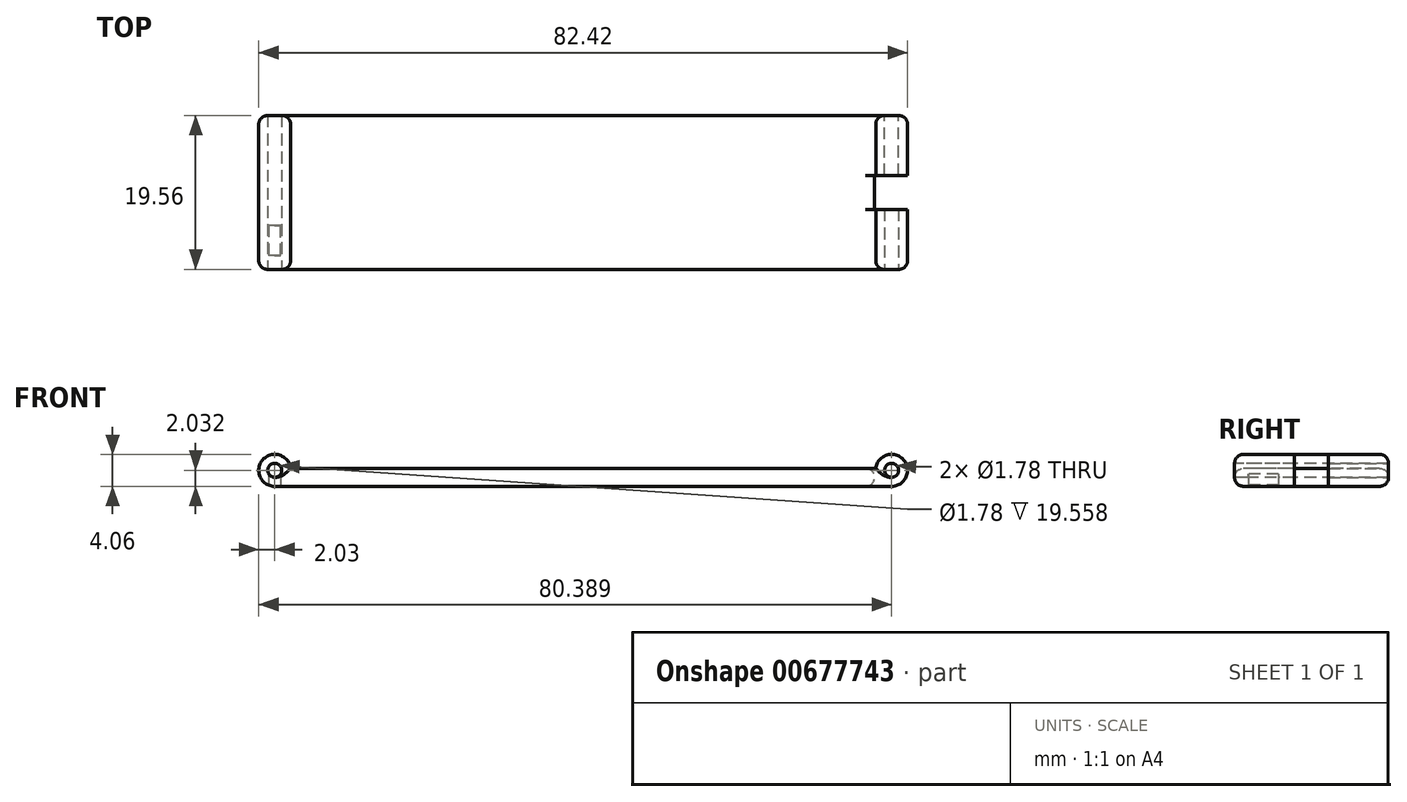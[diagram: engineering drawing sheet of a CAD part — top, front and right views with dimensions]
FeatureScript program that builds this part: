
annotation { "Feature Type Name" : "Feature", "Feature Type Description" : "" }
export const myFeature = defineFeature(function(context is Context, id is Id, definition is map)
    precondition{}
    {
        {
            var Q0;
            Q0=qCreatedBy(makeId("Top.planeOp"),FACE);
            var sketch = newSketch(context, id + "F0", { "sketchPlane" : qUnion([Q0])});
            skLineSegment(sketch, "E0.bottom", {"start": v(0, 0) * mm, "end": v(115.57, 0) * mm});
            skLineSegment(sketch, "E0.top", {"start": v(0, 19.56) * mm, "end": v(115.57, 19.56) * mm});
            skLineSegment(sketch, "E0.left", {"start": v(0, 0) * mm, "end": v(0, 19.56) * mm});
            skLineSegment(sketch, "E0.right", {"start": v(121.92, 6.35) * mm, "end": v(121.92, 13.2) * mm});
            skPoint(sketch, "E1.visualSharp", {"position": v(121.92, 19.56) * mm});
            skArc(sketch, "E1.filletArc", {"start": v(121.92, 13.2) * mm, "mid": v(120.06, 17.7) * mm, "end": v(115.57, 19.56) * mm});
            skPoint(sketch, "E2.visualSharp", {"position": v(121.92, 0) * mm});
            skArc(sketch, "E2.filletArc", {"start": v(115.57, 0) * mm, "mid": v(120.06, 1.86) * mm, "end": v(121.92, 6.35) * mm});
            skLineSegment(sketch, "E3.bottom", {"start": v(24.13, 7.87) * mm, "end": v(22.86, 7.87) * mm});
            skLineSegment(sketch, "E3.top", {"start": v(24.13, 11.68) * mm, "end": v(22.86, 11.68) * mm});
            skLineSegment(sketch, "E3.left", {"start": v(24.77, 8.5) * mm, "end": v(24.77, 11.05) * mm});
            skLineSegment(sketch, "E3.right", {"start": v(22.23, 8.5) * mm, "end": v(22.23, 11.05) * mm});
            skPoint(sketch, "E3.middle", {"position": v(23.5, 9.78) * mm});
            skPoint(sketch, "E3.middle.positionSnap0", {"position": v(0, 9.78) * mm});
            skPoint(sketch, "E3.centerSnap0", {"position": v(0, 9.78) * mm});
            skPoint(sketch, "E4.visualSharp", {"position": v(22.23, 11.68) * mm});
            skArc(sketch, "E4.filletArc", {"start": v(22.86, 11.68) * mm, "mid": v(22.41, 11.5) * mm, "end": v(22.22, 11.05) * mm});
            skPoint(sketch, "E5.visualSharp", {"position": v(24.77, 11.68) * mm});
            skArc(sketch, "E5.filletArc", {"start": v(24.77, 11.05) * mm, "mid": v(24.58, 11.5) * mm, "end": v(24.13, 11.68) * mm});
            skPoint(sketch, "E6.visualSharp", {"position": v(24.77, 7.87) * mm});
            skArc(sketch, "E6.filletArc", {"start": v(24.13, 7.87) * mm, "mid": v(24.58, 8.06) * mm, "end": v(24.77, 8.5) * mm});
            skPoint(sketch, "E7.visualSharp", {"position": v(22.23, 7.87) * mm});
            skArc(sketch, "E7.filletArc", {"start": v(22.23, 8.5) * mm, "mid": v(22.41, 8.06) * mm, "end": v(22.86, 7.87) * mm});
            skPoint(sketch, "E8.1.0.0", {"position": v(28.58, 7.87) * mm});
            skPoint(sketch, "E8.1.0.1", {"position": v(31.12, 7.87) * mm});
            skPoint(sketch, "E8.1.0.2", {"position": v(28.58, 11.68) * mm});
            skPoint(sketch, "E8.1.0.3", {"position": v(31.12, 11.68) * mm});
            skPoint(sketch, "E8.1.0.4", {"position": v(29.85, 9.78) * mm});
            skLineSegment(sketch, "E8.1.0.5", {"start": v(30.48, 11.68) * mm, "end": v(29.21, 11.68) * mm});
            skLineSegment(sketch, "E8.1.0.6", {"start": v(31.12, 8.5) * mm, "end": v(31.12, 11.05) * mm});
            skLineSegment(sketch, "E8.1.0.7", {"start": v(28.58, 8.5) * mm, "end": v(28.58, 11.05) * mm});
            skArc(sketch, "E8.1.0.8", {"start": v(31.12, 11.05) * mm, "mid": v(30.93, 11.5) * mm, "end": v(30.48, 11.68) * mm});
            skArc(sketch, "E8.1.0.9", {"start": v(29.21, 11.68) * mm, "mid": v(28.76, 11.5) * mm, "end": v(28.57, 11.05) * mm});
            skArc(sketch, "E8.1.0.10", {"start": v(30.48, 7.87) * mm, "mid": v(30.93, 8.06) * mm, "end": v(31.12, 8.5) * mm});
            skLineSegment(sketch, "E8.1.0.11", {"start": v(30.48, 7.87) * mm, "end": v(29.21, 7.87) * mm});
            skArc(sketch, "E8.1.0.12", {"start": v(28.58, 8.5) * mm, "mid": v(28.76, 8.06) * mm, "end": v(29.21, 7.87) * mm});
            skPoint(sketch, "E8.2.0.0", {"position": v(34.93, 7.87) * mm});
            skPoint(sketch, "E8.2.0.1", {"position": v(37.47, 7.87) * mm});
            skPoint(sketch, "E8.2.0.2", {"position": v(34.93, 11.68) * mm});
            skPoint(sketch, "E8.2.0.3", {"position": v(37.47, 11.68) * mm});
            skPoint(sketch, "E8.2.0.4", {"position": v(36.2, 9.78) * mm});
            skLineSegment(sketch, "E8.2.0.5", {"start": v(36.83, 11.68) * mm, "end": v(35.56, 11.68) * mm});
            skLineSegment(sketch, "E8.2.0.6", {"start": v(37.47, 8.5) * mm, "end": v(37.47, 11.05) * mm});
            skLineSegment(sketch, "E8.2.0.7", {"start": v(34.93, 8.5) * mm, "end": v(34.93, 11.05) * mm});
            skArc(sketch, "E8.2.0.8", {"start": v(37.46, 11.05) * mm, "mid": v(37.28, 11.5) * mm, "end": v(36.83, 11.68) * mm});
            skArc(sketch, "E8.2.0.9", {"start": v(35.56, 11.68) * mm, "mid": v(35.11, 11.5) * mm, "end": v(34.92, 11.05) * mm});
            skArc(sketch, "E8.2.0.10", {"start": v(36.83, 7.87) * mm, "mid": v(37.28, 8.06) * mm, "end": v(37.47, 8.5) * mm});
            skLineSegment(sketch, "E8.2.0.11", {"start": v(36.83, 7.87) * mm, "end": v(35.56, 7.87) * mm});
            skArc(sketch, "E8.2.0.12", {"start": v(34.93, 8.5) * mm, "mid": v(35.11, 8.06) * mm, "end": v(35.56, 7.87) * mm});
            skPoint(sketch, "E8.3.0.0", {"position": v(41.28, 7.87) * mm});
            skPoint(sketch, "E8.3.0.1", {"position": v(43.82, 7.87) * mm});
            skPoint(sketch, "E8.3.0.2", {"position": v(41.28, 11.68) * mm});
            skPoint(sketch, "E8.3.0.3", {"position": v(43.82, 11.68) * mm});
            skPoint(sketch, "E8.3.0.4", {"position": v(42.55, 9.78) * mm});
            skLineSegment(sketch, "E8.3.0.5", {"start": v(43.18, 11.68) * mm, "end": v(41.91, 11.68) * mm});
            skLineSegment(sketch, "E8.3.0.6", {"start": v(43.82, 8.5) * mm, "end": v(43.82, 11.05) * mm});
            skLineSegment(sketch, "E8.3.0.7", {"start": v(41.28, 8.5) * mm, "end": v(41.28, 11.05) * mm});
            skArc(sketch, "E8.3.0.8", {"start": v(43.82, 11.05) * mm, "mid": v(43.63, 11.5) * mm, "end": v(43.18, 11.68) * mm});
            skArc(sketch, "E8.3.0.9", {"start": v(41.91, 11.68) * mm, "mid": v(41.46, 11.5) * mm, "end": v(41.28, 11.05) * mm});
            skArc(sketch, "E8.3.0.10", {"start": v(43.18, 7.87) * mm, "mid": v(43.63, 8.06) * mm, "end": v(43.82, 8.5) * mm});
            skLineSegment(sketch, "E8.3.0.11", {"start": v(43.18, 7.87) * mm, "end": v(41.91, 7.87) * mm});
            skArc(sketch, "E8.3.0.12", {"start": v(41.28, 8.5) * mm, "mid": v(41.46, 8.06) * mm, "end": v(41.91, 7.87) * mm});
            skPoint(sketch, "E8.4.0.0", {"position": v(47.63, 7.87) * mm});
            skPoint(sketch, "E8.4.0.1", {"position": v(50.17, 7.87) * mm});
            skPoint(sketch, "E8.4.0.2", {"position": v(47.63, 11.68) * mm});
            skPoint(sketch, "E8.4.0.3", {"position": v(50.17, 11.68) * mm});
            skPoint(sketch, "E8.4.0.4", {"position": v(48.9, 9.78) * mm});
            skLineSegment(sketch, "E8.4.0.5", {"start": v(49.53, 11.68) * mm, "end": v(48.26, 11.68) * mm});
            skLineSegment(sketch, "E8.4.0.6", {"start": v(50.17, 8.5) * mm, "end": v(50.17, 11.05) * mm});
            skLineSegment(sketch, "E8.4.0.7", {"start": v(47.63, 8.5) * mm, "end": v(47.63, 11.05) * mm});
            skArc(sketch, "E8.4.0.8", {"start": v(50.16, 11.05) * mm, "mid": v(49.98, 11.5) * mm, "end": v(49.53, 11.68) * mm});
            skArc(sketch, "E8.4.0.9", {"start": v(48.26, 11.68) * mm, "mid": v(47.81, 11.5) * mm, "end": v(47.62, 11.05) * mm});
            skArc(sketch, "E8.4.0.10", {"start": v(49.53, 7.87) * mm, "mid": v(49.98, 8.06) * mm, "end": v(50.17, 8.5) * mm});
            skLineSegment(sketch, "E8.4.0.11", {"start": v(49.53, 7.87) * mm, "end": v(48.26, 7.87) * mm});
            skArc(sketch, "E8.4.0.12", {"start": v(47.63, 8.5) * mm, "mid": v(47.81, 8.06) * mm, "end": v(48.26, 7.87) * mm});
            skPoint(sketch, "E8.5.0.0", {"position": v(53.98, 7.87) * mm});
            skPoint(sketch, "E8.5.0.1", {"position": v(56.52, 7.87) * mm});
            skPoint(sketch, "E8.5.0.2", {"position": v(53.98, 11.68) * mm});
            skPoint(sketch, "E8.5.0.3", {"position": v(56.52, 11.68) * mm});
            skPoint(sketch, "E8.5.0.4", {"position": v(55.25, 9.78) * mm});
            skLineSegment(sketch, "E8.5.0.5", {"start": v(55.88, 11.68) * mm, "end": v(54.61, 11.68) * mm});
            skLineSegment(sketch, "E8.5.0.6", {"start": v(56.52, 8.5) * mm, "end": v(56.52, 11.05) * mm});
            skLineSegment(sketch, "E8.5.0.7", {"start": v(53.98, 8.5) * mm, "end": v(53.98, 11.05) * mm});
            skArc(sketch, "E8.5.0.8", {"start": v(56.52, 11.05) * mm, "mid": v(56.33, 11.5) * mm, "end": v(55.88, 11.68) * mm});
            skArc(sketch, "E8.5.0.9", {"start": v(54.61, 11.68) * mm, "mid": v(54.16, 11.5) * mm, "end": v(53.98, 11.05) * mm});
            skArc(sketch, "E8.5.0.10", {"start": v(55.88, 7.87) * mm, "mid": v(56.33, 8.06) * mm, "end": v(56.52, 8.5) * mm});
            skLineSegment(sketch, "E8.5.0.11", {"start": v(55.88, 7.87) * mm, "end": v(54.61, 7.87) * mm});
            skArc(sketch, "E8.5.0.12", {"start": v(53.98, 8.5) * mm, "mid": v(54.16, 8.06) * mm, "end": v(54.61, 7.87) * mm});
            skPoint(sketch, "E8.6.0.0", {"position": v(60.33, 7.87) * mm});
            skPoint(sketch, "E8.6.0.1", {"position": v(62.87, 7.87) * mm});
            skPoint(sketch, "E8.6.0.2", {"position": v(60.33, 11.68) * mm});
            skPoint(sketch, "E8.6.0.3", {"position": v(62.87, 11.68) * mm});
            skPoint(sketch, "E8.6.0.4", {"position": v(61.6, 9.78) * mm});
            skLineSegment(sketch, "E8.6.0.5", {"start": v(62.23, 11.68) * mm, "end": v(60.96, 11.68) * mm});
            skLineSegment(sketch, "E8.6.0.6", {"start": v(62.87, 8.5) * mm, "end": v(62.87, 11.05) * mm});
            skLineSegment(sketch, "E8.6.0.7", {"start": v(60.33, 8.5) * mm, "end": v(60.33, 11.05) * mm});
            skArc(sketch, "E8.6.0.8", {"start": v(62.87, 11.05) * mm, "mid": v(62.68, 11.5) * mm, "end": v(62.23, 11.68) * mm});
            skArc(sketch, "E8.6.0.9", {"start": v(60.96, 11.68) * mm, "mid": v(60.51, 11.5) * mm, "end": v(60.33, 11.05) * mm});
            skArc(sketch, "E8.6.0.10", {"start": v(62.23, 7.87) * mm, "mid": v(62.68, 8.06) * mm, "end": v(62.87, 8.5) * mm});
            skLineSegment(sketch, "E8.6.0.11", {"start": v(62.23, 7.87) * mm, "end": v(60.96, 7.87) * mm});
            skArc(sketch, "E8.6.0.12", {"start": v(60.33, 8.5) * mm, "mid": v(60.51, 8.06) * mm, "end": v(60.96, 7.87) * mm});
            skPoint(sketch, "E8.7.0.0", {"position": v(66.68, 7.87) * mm});
            skPoint(sketch, "E8.7.0.1", {"position": v(69.22, 7.87) * mm});
            skPoint(sketch, "E8.7.0.2", {"position": v(66.68, 11.68) * mm});
            skPoint(sketch, "E8.7.0.3", {"position": v(69.22, 11.68) * mm});
            skPoint(sketch, "E8.7.0.4", {"position": v(67.95, 9.78) * mm});
            skLineSegment(sketch, "E8.7.0.5", {"start": v(68.58, 11.68) * mm, "end": v(67.31, 11.68) * mm});
            skLineSegment(sketch, "E8.7.0.6", {"start": v(69.22, 8.5) * mm, "end": v(69.22, 11.05) * mm});
            skLineSegment(sketch, "E8.7.0.7", {"start": v(66.68, 8.5) * mm, "end": v(66.68, 11.05) * mm});
            skArc(sketch, "E8.7.0.8", {"start": v(69.22, 11.05) * mm, "mid": v(69.03, 11.5) * mm, "end": v(68.58, 11.68) * mm});
            skArc(sketch, "E8.7.0.9", {"start": v(67.31, 11.68) * mm, "mid": v(66.86, 11.5) * mm, "end": v(66.68, 11.05) * mm});
            skArc(sketch, "E8.7.0.10", {"start": v(68.58, 7.87) * mm, "mid": v(69.03, 8.06) * mm, "end": v(69.22, 8.5) * mm});
            skLineSegment(sketch, "E8.7.0.11", {"start": v(68.58, 7.87) * mm, "end": v(67.31, 7.87) * mm});
            skArc(sketch, "E8.7.0.12", {"start": v(66.68, 8.5) * mm, "mid": v(66.86, 8.06) * mm, "end": v(67.31, 7.87) * mm});
            skPoint(sketch, "E8.8.0.0", {"position": v(73.03, 7.87) * mm});
            skPoint(sketch, "E8.8.0.1", {"position": v(75.57, 7.87) * mm});
            skPoint(sketch, "E8.8.0.2", {"position": v(73.03, 11.68) * mm});
            skPoint(sketch, "E8.8.0.3", {"position": v(75.57, 11.68) * mm});
            skPoint(sketch, "E8.8.0.4", {"position": v(74.3, 9.78) * mm});
            skLineSegment(sketch, "E8.8.0.5", {"start": v(74.93, 11.68) * mm, "end": v(73.66, 11.68) * mm});
            skLineSegment(sketch, "E8.8.0.6", {"start": v(75.57, 8.5) * mm, "end": v(75.57, 11.05) * mm});
            skLineSegment(sketch, "E8.8.0.7", {"start": v(73.03, 8.5) * mm, "end": v(73.03, 11.05) * mm});
            skArc(sketch, "E8.8.0.8", {"start": v(75.57, 11.05) * mm, "mid": v(75.38, 11.5) * mm, "end": v(74.93, 11.68) * mm});
            skArc(sketch, "E8.8.0.9", {"start": v(73.66, 11.68) * mm, "mid": v(73.21, 11.5) * mm, "end": v(73.03, 11.05) * mm});
            skArc(sketch, "E8.8.0.10", {"start": v(74.93, 7.87) * mm, "mid": v(75.38, 8.06) * mm, "end": v(75.57, 8.5) * mm});
            skLineSegment(sketch, "E8.8.0.11", {"start": v(74.93, 7.87) * mm, "end": v(73.66, 7.87) * mm});
            skArc(sketch, "E8.8.0.12", {"start": v(73.03, 8.5) * mm, "mid": v(73.21, 8.06) * mm, "end": v(73.66, 7.87) * mm});
            skPoint(sketch, "E8.9.0.0", {"position": v(79.38, 7.87) * mm});
            skPoint(sketch, "E8.9.0.1", {"position": v(81.92, 7.87) * mm});
            skPoint(sketch, "E8.9.0.2", {"position": v(79.38, 11.68) * mm});
            skPoint(sketch, "E8.9.0.3", {"position": v(81.92, 11.68) * mm});
            skPoint(sketch, "E8.9.0.4", {"position": v(80.65, 9.78) * mm});
            skLineSegment(sketch, "E8.9.0.5", {"start": v(81.28, 11.68) * mm, "end": v(80.01, 11.68) * mm});
            skLineSegment(sketch, "E8.9.0.6", {"start": v(81.92, 8.5) * mm, "end": v(81.92, 11.05) * mm});
            skLineSegment(sketch, "E8.9.0.7", {"start": v(79.38, 8.5) * mm, "end": v(79.38, 11.05) * mm});
            skArc(sketch, "E8.9.0.8", {"start": v(81.92, 11.05) * mm, "mid": v(81.73, 11.5) * mm, "end": v(81.28, 11.68) * mm});
            skArc(sketch, "E8.9.0.9", {"start": v(80.01, 11.68) * mm, "mid": v(79.56, 11.5) * mm, "end": v(79.38, 11.05) * mm});
            skArc(sketch, "E8.9.0.10", {"start": v(81.28, 7.87) * mm, "mid": v(81.73, 8.06) * mm, "end": v(81.92, 8.5) * mm});
            skLineSegment(sketch, "E8.9.0.11", {"start": v(81.28, 7.87) * mm, "end": v(80.01, 7.87) * mm});
            skArc(sketch, "E8.9.0.12", {"start": v(79.38, 8.5) * mm, "mid": v(79.56, 8.06) * mm, "end": v(80.01, 7.87) * mm});
            skPoint(sketch, "E8.10.0.0", {"position": v(85.73, 7.87) * mm});
            skPoint(sketch, "E8.10.0.1", {"position": v(88.27, 7.87) * mm});
            skPoint(sketch, "E8.10.0.2", {"position": v(85.73, 11.68) * mm});
            skPoint(sketch, "E8.10.0.3", {"position": v(88.27, 11.68) * mm});
            skPoint(sketch, "E8.10.0.4", {"position": v(87, 9.78) * mm});
            skLineSegment(sketch, "E8.10.0.5", {"start": v(87.63, 11.68) * mm, "end": v(86.36, 11.68) * mm});
            skLineSegment(sketch, "E8.10.0.6", {"start": v(88.27, 8.5) * mm, "end": v(88.27, 11.05) * mm});
            skLineSegment(sketch, "E8.10.0.7", {"start": v(85.73, 8.5) * mm, "end": v(85.73, 11.05) * mm});
            skArc(sketch, "E8.10.0.8", {"start": v(88.27, 11.05) * mm, "mid": v(88.08, 11.5) * mm, "end": v(87.63, 11.68) * mm});
            skArc(sketch, "E8.10.0.9", {"start": v(86.36, 11.68) * mm, "mid": v(85.91, 11.5) * mm, "end": v(85.73, 11.05) * mm});
            skArc(sketch, "E8.10.0.10", {"start": v(87.63, 7.87) * mm, "mid": v(88.08, 8.06) * mm, "end": v(88.27, 8.5) * mm});
            skLineSegment(sketch, "E8.10.0.11", {"start": v(87.63, 7.87) * mm, "end": v(86.36, 7.87) * mm});
            skArc(sketch, "E8.10.0.12", {"start": v(85.73, 8.5) * mm, "mid": v(85.91, 8.06) * mm, "end": v(86.36, 7.87) * mm});
            skPoint(sketch, "E8.11.0.0", {"position": v(92.08, 7.87) * mm});
            skPoint(sketch, "E8.11.0.1", {"position": v(94.62, 7.87) * mm});
            skPoint(sketch, "E8.11.0.2", {"position": v(92.08, 11.68) * mm});
            skPoint(sketch, "E8.11.0.3", {"position": v(94.62, 11.68) * mm});
            skPoint(sketch, "E8.11.0.4", {"position": v(93.35, 9.78) * mm});
            skLineSegment(sketch, "E8.11.0.5", {"start": v(93.98, 11.68) * mm, "end": v(92.71, 11.68) * mm});
            skLineSegment(sketch, "E8.11.0.6", {"start": v(94.62, 8.5) * mm, "end": v(94.62, 11.05) * mm});
            skLineSegment(sketch, "E8.11.0.7", {"start": v(92.08, 8.5) * mm, "end": v(92.08, 11.05) * mm});
            skArc(sketch, "E8.11.0.8", {"start": v(94.62, 11.05) * mm, "mid": v(94.43, 11.5) * mm, "end": v(93.98, 11.68) * mm});
            skArc(sketch, "E8.11.0.9", {"start": v(92.71, 11.68) * mm, "mid": v(92.26, 11.5) * mm, "end": v(92.08, 11.05) * mm});
            skArc(sketch, "E8.11.0.10", {"start": v(93.98, 7.87) * mm, "mid": v(94.43, 8.06) * mm, "end": v(94.62, 8.5) * mm});
            skLineSegment(sketch, "E8.11.0.11", {"start": v(93.98, 7.87) * mm, "end": v(92.71, 7.87) * mm});
            skArc(sketch, "E8.11.0.12", {"start": v(92.08, 8.5) * mm, "mid": v(92.26, 8.06) * mm, "end": v(92.71, 7.87) * mm});
            skPoint(sketch, "E8.12.0.0", {"position": v(98.43, 7.87) * mm});
            skPoint(sketch, "E8.12.0.1", {"position": v(100.97, 7.87) * mm});
            skPoint(sketch, "E8.12.0.2", {"position": v(98.43, 11.68) * mm});
            skPoint(sketch, "E8.12.0.3", {"position": v(100.97, 11.68) * mm});
            skPoint(sketch, "E8.12.0.4", {"position": v(99.7, 9.78) * mm});
            skLineSegment(sketch, "E8.12.0.5", {"start": v(100.33, 11.68) * mm, "end": v(99.06, 11.68) * mm});
            skLineSegment(sketch, "E8.12.0.6", {"start": v(100.97, 8.5) * mm, "end": v(100.97, 11.05) * mm});
            skLineSegment(sketch, "E8.12.0.7", {"start": v(98.43, 8.5) * mm, "end": v(98.43, 11.05) * mm});
            skArc(sketch, "E8.12.0.8", {"start": v(100.97, 11.05) * mm, "mid": v(100.78, 11.5) * mm, "end": v(100.33, 11.68) * mm});
            skArc(sketch, "E8.12.0.9", {"start": v(99.06, 11.68) * mm, "mid": v(98.61, 11.5) * mm, "end": v(98.43, 11.05) * mm});
            skArc(sketch, "E8.12.0.10", {"start": v(100.33, 7.87) * mm, "mid": v(100.78, 8.06) * mm, "end": v(100.97, 8.5) * mm});
            skLineSegment(sketch, "E8.12.0.11", {"start": v(100.33, 7.87) * mm, "end": v(99.06, 7.87) * mm});
            skArc(sketch, "E8.12.0.12", {"start": v(98.43, 8.5) * mm, "mid": v(98.61, 8.06) * mm, "end": v(99.06, 7.87) * mm});
            skLineSegment(sketch, "E8.direction1", {"start": v(22.23, 7.87) * mm, "end": v(28.58, 7.87) * mm, "construction": true});
            skSolve(sketch);
        }
        {
            var Q0;
            Q0=makeQuery(id+"F0.imprint","IMPRINT",FACE,{"disambiguationData":[TD([[makeQuery(id+"F0.imprint","IMPRINT",EDGE,{"derivedFrom":sQuery(id+"F0.wireOp",EDGE,"E0.bottom")}),1.0]])]});
            extrude(context, id + "F1", {"entities" : qUnion([Q0]), "depth" : 2.3 * mm, "offsetDistance" : 25.4 * mm});
        }
        {
            var Q0;
            Q0=makeQuery(id+"F1.opExtrude","SWEPT_FACE",FACE,{"disambiguationData":[OSD([sQuery(id+"F0.wireOp",EDGE,"E0.bottom")])]});
            var sketch = newSketch(context, id + "F2", { "sketchPlane" : qUnion([Q0])});
            skCircle(sketch, "E9", {"center": v(0, 2.03) * mm, "radius": 0.89 * mm});
            skCircle(sketch, "E10.0", {"center": v(0, 2.03) * mm, "radius": 2.03 * mm});
            skSolve(sketch);
        }
        {
            var Q0;
            {var subQ0=sQuery(id+"F2.wireOp",EDGE,"E9");var subQ1=makeQuery(id+"F1.opExtrude","SWEPT_EDGE",EDGE,{"disambiguationData":[OSD([sQuery(id+"F0.wireOp",EDGE,"E0.bottom"),sQuery(id+"F0.wireOp",EDGE,"E0.left")])]});var subQ2=makeQuery(id+"F2.imprint","INTERSECT",VERTEX,{"disambiguationData":[OD(0.0)],"derivedFrom":[subQ1,subQ0]});Q0=makeQuery(id+"F2.imprint","IMPRINT",FACE,{"disambiguationData":[TD([[makeQuery(id+"F2.imprint","IMPRINT",EDGE,{"disambiguationData":[TD([[subQ2,-1.0]])],"derivedFrom":subQ0}),1.0]])]});}
            extrude(context, id + "F3", {"entities" : qUnion([Q0]), "operationType" : NewBodyOperationType.REMOVE, "endBound" : BoundingType.THROUGH_ALL, "oppositeDirection" : true, "depth" : 25.4 * mm, "offsetDistance" : 25.4 * mm});
        }
        {
            var Q0;
            {var subQ0=sQuery(id+"F0.wireOp",EDGE,"E0.bottom");var subQ6=sQuery(id+"F2.wireOp",EDGE,"E10.0");var subQ7=makeQuery(id+"F1.opExtrude","CAP_EDGE",EDGE,{"disambiguationData":[OSD([subQ0])],"isStart":true});var subQ8=makeQuery(id+"F2.imprint","INTERSECT",VERTEX,{"derivedFrom":[subQ7,subQ6]});Q0=makeQuery(id+"F2.imprint","IMPRINT",FACE,{"disambiguationData":[TD([[makeQuery(id+"F2.imprint","IMPRINT",EDGE,{"disambiguationData":[TD([[subQ8,1.0]])],"derivedFrom":subQ6}),1.0]])]});}
            var Q1;
            Q1=makeQuery(id+"F1.opExtrude","SWEPT_FACE",FACE,{"disambiguationData":[OSD([sQuery(id+"F0.wireOp",EDGE,"E0.top")])]});
            extrude(context, id + "F4", {"entities" : qUnion([Q0]), "operationType" : NewBodyOperationType.ADD, "endBound" : BoundingType.UP_TO_SURFACE, "oppositeDirection" : true, "depth" : 25.4 * mm, "endBoundEntityFace" : qUnion([Q1]), "offsetDistance" : 25.4 * mm});
        }
        {
            var Q0;
            Q0=makeQuery(id+"F1.opExtrude","CAP_FACE",FACE,{"disambiguationData":[OSD([sQuery(id+"F0.wireOp",EDGE,"E0.bottom"),sQuery(id+"F0.wireOp",EDGE,"E0.top"),sQuery(id+"F0.wireOp",EDGE,"E0.left"),sQuery(id+"F0.wireOp",EDGE,"E0.right"),sQuery(id+"F0.wireOp",EDGE,"E1.filletArc"),sQuery(id+"F0.wireOp",EDGE,"E2.filletArc"),sQuery(id+"F0.wireOp",EDGE,"E3.bottom"),sQuery(id+"F0.wireOp",EDGE,"E3.top"),sQuery(id+"F0.wireOp",EDGE,"E3.left"),sQuery(id+"F0.wireOp",EDGE,"E3.right"),sQuery(id+"F0.wireOp",EDGE,"E4.filletArc"),sQuery(id+"F0.wireOp",EDGE,"E5.filletArc"),sQuery(id+"F0.wireOp",EDGE,"E6.filletArc"),sQuery(id+"F0.wireOp",EDGE,"E7.filletArc"),sQuery(id+"F0.wireOp",EDGE,"E8.1.0.5"),sQuery(id+"F0.wireOp",EDGE,"E8.1.0.6"),sQuery(id+"F0.wireOp",EDGE,"E8.1.0.7"),sQuery(id+"F0.wireOp",EDGE,"E8.1.0.8"),sQuery(id+"F0.wireOp",EDGE,"E8.1.0.9"),sQuery(id+"F0.wireOp",EDGE,"E8.1.0.10"),sQuery(id+"F0.wireOp",EDGE,"E8.1.0.11"),sQuery(id+"F0.wireOp",EDGE,"E8.1.0.12"),sQuery(id+"F0.wireOp",EDGE,"E8.2.0.5"),sQuery(id+"F0.wireOp",EDGE,"E8.2.0.6"),sQuery(id+"F0.wireOp",EDGE,"E8.2.0.7"),sQuery(id+"F0.wireOp",EDGE,"E8.2.0.8"),sQuery(id+"F0.wireOp",EDGE,"E8.2.0.9"),sQuery(id+"F0.wireOp",EDGE,"E8.2.0.10"),sQuery(id+"F0.wireOp",EDGE,"E8.2.0.11"),sQuery(id+"F0.wireOp",EDGE,"E8.2.0.12"),sQuery(id+"F0.wireOp",EDGE,"E8.3.0.5"),sQuery(id+"F0.wireOp",EDGE,"E8.3.0.6"),sQuery(id+"F0.wireOp",EDGE,"E8.3.0.7"),sQuery(id+"F0.wireOp",EDGE,"E8.3.0.8"),sQuery(id+"F0.wireOp",EDGE,"E8.3.0.9"),sQuery(id+"F0.wireOp",EDGE,"E8.3.0.10"),sQuery(id+"F0.wireOp",EDGE,"E8.3.0.11"),sQuery(id+"F0.wireOp",EDGE,"E8.3.0.12"),sQuery(id+"F0.wireOp",EDGE,"E8.4.0.5"),sQuery(id+"F0.wireOp",EDGE,"E8.4.0.6"),sQuery(id+"F0.wireOp",EDGE,"E8.4.0.7"),sQuery(id+"F0.wireOp",EDGE,"E8.4.0.8"),sQuery(id+"F0.wireOp",EDGE,"E8.4.0.9"),sQuery(id+"F0.wireOp",EDGE,"E8.4.0.10"),sQuery(id+"F0.wireOp",EDGE,"E8.4.0.11"),sQuery(id+"F0.wireOp",EDGE,"E8.4.0.12"),sQuery(id+"F0.wireOp",EDGE,"E8.5.0.5"),sQuery(id+"F0.wireOp",EDGE,"E8.5.0.6"),sQuery(id+"F0.wireOp",EDGE,"E8.5.0.7"),sQuery(id+"F0.wireOp",EDGE,"E8.5.0.8"),sQuery(id+"F0.wireOp",EDGE,"E8.5.0.9"),sQuery(id+"F0.wireOp",EDGE,"E8.5.0.10"),sQuery(id+"F0.wireOp",EDGE,"E8.5.0.11"),sQuery(id+"F0.wireOp",EDGE,"E8.5.0.12"),sQuery(id+"F0.wireOp",EDGE,"E8.6.0.5"),sQuery(id+"F0.wireOp",EDGE,"E8.6.0.6"),sQuery(id+"F0.wireOp",EDGE,"E8.6.0.7"),sQuery(id+"F0.wireOp",EDGE,"E8.6.0.8"),sQuery(id+"F0.wireOp",EDGE,"E8.6.0.9"),sQuery(id+"F0.wireOp",EDGE,"E8.6.0.10"),sQuery(id+"F0.wireOp",EDGE,"E8.6.0.11"),sQuery(id+"F0.wireOp",EDGE,"E8.6.0.12"),sQuery(id+"F0.wireOp",EDGE,"E8.7.0.5"),sQuery(id+"F0.wireOp",EDGE,"E8.7.0.6"),sQuery(id+"F0.wireOp",EDGE,"E8.7.0.7"),sQuery(id+"F0.wireOp",EDGE,"E8.7.0.8"),sQuery(id+"F0.wireOp",EDGE,"E8.7.0.9"),sQuery(id+"F0.wireOp",EDGE,"E8.7.0.10"),sQuery(id+"F0.wireOp",EDGE,"E8.7.0.11"),sQuery(id+"F0.wireOp",EDGE,"E8.7.0.12"),sQuery(id+"F0.wireOp",EDGE,"E8.8.0.5"),sQuery(id+"F0.wireOp",EDGE,"E8.8.0.6"),sQuery(id+"F0.wireOp",EDGE,"E8.8.0.7"),sQuery(id+"F0.wireOp",EDGE,"E8.8.0.8"),sQuery(id+"F0.wireOp",EDGE,"E8.8.0.9"),sQuery(id+"F0.wireOp",EDGE,"E8.8.0.10"),sQuery(id+"F0.wireOp",EDGE,"E8.8.0.11"),sQuery(id+"F0.wireOp",EDGE,"E8.8.0.12"),sQuery(id+"F0.wireOp",EDGE,"E8.9.0.5"),sQuery(id+"F0.wireOp",EDGE,"E8.9.0.6"),sQuery(id+"F0.wireOp",EDGE,"E8.9.0.7"),sQuery(id+"F0.wireOp",EDGE,"E8.9.0.8"),sQuery(id+"F0.wireOp",EDGE,"E8.9.0.9"),sQuery(id+"F0.wireOp",EDGE,"E8.9.0.10"),sQuery(id+"F0.wireOp",EDGE,"E8.9.0.11"),sQuery(id+"F0.wireOp",EDGE,"E8.9.0.12"),sQuery(id+"F0.wireOp",EDGE,"E8.10.0.5"),sQuery(id+"F0.wireOp",EDGE,"E8.10.0.6"),sQuery(id+"F0.wireOp",EDGE,"E8.10.0.7"),sQuery(id+"F0.wireOp",EDGE,"E8.10.0.8"),sQuery(id+"F0.wireOp",EDGE,"E8.10.0.9"),sQuery(id+"F0.wireOp",EDGE,"E8.10.0.10"),sQuery(id+"F0.wireOp",EDGE,"E8.10.0.11"),sQuery(id+"F0.wireOp",EDGE,"E8.10.0.12"),sQuery(id+"F0.wireOp",EDGE,"E8.11.0.5"),sQuery(id+"F0.wireOp",EDGE,"E8.11.0.6"),sQuery(id+"F0.wireOp",EDGE,"E8.11.0.7"),sQuery(id+"F0.wireOp",EDGE,"E8.11.0.8"),sQuery(id+"F0.wireOp",EDGE,"E8.11.0.9"),sQuery(id+"F0.wireOp",EDGE,"E8.11.0.10"),sQuery(id+"F0.wireOp",EDGE,"E8.11.0.11"),sQuery(id+"F0.wireOp",EDGE,"E8.11.0.12"),sQuery(id+"F0.wireOp",EDGE,"E8.12.0.5"),sQuery(id+"F0.wireOp",EDGE,"E8.12.0.6"),sQuery(id+"F0.wireOp",EDGE,"E8.12.0.7"),sQuery(id+"F0.wireOp",EDGE,"E8.12.0.8"),sQuery(id+"F0.wireOp",EDGE,"E8.12.0.9"),sQuery(id+"F0.wireOp",EDGE,"E8.12.0.10"),sQuery(id+"F0.wireOp",EDGE,"E8.12.0.11"),sQuery(id+"F0.wireOp",EDGE,"E8.12.0.12")])],"isStart":true});
            var sketch = newSketch(context, id + "F5", { "sketchPlane" : qUnion([Q0])});
            skLineSegment(sketch, "E11.bottom", {"start": v(-0.76, -1.78) * mm, "end": v(0.76, -1.78) * mm});
            skLineSegment(sketch, "E11.top", {"start": v(-0.76, -5.59) * mm, "end": v(0.76, -5.59) * mm});
            skLineSegment(sketch, "E11.left", {"start": v(-0.76, -1.78) * mm, "end": v(-0.76, -5.59) * mm});
            skLineSegment(sketch, "E11.right", {"start": v(0.76, -1.78) * mm, "end": v(0.76, -5.59) * mm});
            skPoint(sketch, "E11.middle", {"position": v(0, -3.68) * mm});
            skSolve(sketch);
        }
        {
            var Q0;
            {var subQ0=sQuery(id+"F5.wireOp",EDGE,"E11.left");Q0=makeQuery(id+"F5.imprint","IMPRINT",FACE,{"disambiguationData":[TD([[makeQuery(id+"F5.imprint","IMPRINT",EDGE,{"derivedFrom":subQ0}),1.0]])]});}
            var Q1;
            {var subQ0=sQuery(id+"F5.wireOp",EDGE,"E11.right");Q1=makeQuery(id+"F5.imprint","IMPRINT",FACE,{"disambiguationData":[TD([[makeQuery(id+"F5.imprint","IMPRINT",EDGE,{"derivedFrom":subQ0}),-1.0]])]});}
            extrude(context, id + "F6", {"entities" : qUnion([Q0, Q1]), "operationType" : NewBodyOperationType.REMOVE, "endBound" : BoundingType.UP_TO_NEXT, "oppositeDirection" : true, "depth" : 25.4 * mm, "offsetDistance" : 25.4 * mm});
        }
        {
            var Q0;
            Q0=qCreatedBy(makeId("Top.planeOp"),FACE);
            var sketch = newSketch(context, id + "F7", { "sketchPlane" : qUnion([Q0])});
            skLineSegment(sketch, "E12.bottom", {"start": v(0, 25.9) * mm, "end": v(76.2, 25.9) * mm});
            skLineSegment(sketch, "E12.top", {"start": v(0, 45.47) * mm, "end": v(76.2, 45.47) * mm});
            skLineSegment(sketch, "E12.left", {"start": v(0, 25.9) * mm, "end": v(0, 45.47) * mm});
            skLineSegment(sketch, "E12.right", {"start": v(76.2, 25.9) * mm, "end": v(76.2, 45.47) * mm});
            skSolve(sketch);
        }
        {
            var Q0;
            Q0=makeQuery(id+"F7.imprint","IMPRINT",FACE,{"disambiguationData":[TD([[makeQuery(id+"F7.imprint","IMPRINT",EDGE,{"derivedFrom":sQuery(id+"F7.wireOp",EDGE,"E12.bottom")}),1.0]])]});
            extrude(context, id + "F8", {"entities" : qUnion([Q0]), "depth" : 2.3 * mm, "offsetDistance" : 25.4 * mm});
        }
        {
            var Q0;
            Q0=makeQuery(id+"F8.opExtrude","SWEPT_FACE",FACE,{"disambiguationData":[OSD([sQuery(id+"F7.wireOp",EDGE,"E12.bottom")])]});
            var sketch = newSketch(context, id + "F9", { "sketchPlane" : qUnion([Q0])});
            skCircle(sketch, "E13", {"center": v(0, 2.03) * mm, "radius": 2.03 * mm});
            skCircle(sketch, "E14", {"center": v(0, 2.03) * mm, "radius": 0.89 * mm});
            skSolve(sketch);
        }
        {
            var Q0;
            {var subQ0=sQuery(id+"F9.wireOp",EDGE,"E14");var subQ1=sQuery(id+"F7.wireOp",EDGE,"E12.bottom");var subQ4=makeQuery(id+"F8.opExtrude","CAP_EDGE",EDGE,{"disambiguationData":[OSD([subQ1])],"isStart":false});var subQ5=makeQuery(id+"F9.imprint","INTERSECT",VERTEX,{"derivedFrom":[subQ4,subQ0]});Q0=makeQuery(id+"F9.imprint","IMPRINT",FACE,{"disambiguationData":[TD([[makeQuery(id+"F9.imprint","IMPRINT",EDGE,{"disambiguationData":[TD([[subQ5,1.0]])],"derivedFrom":subQ0}),1.0]])]});}
            extrude(context, id + "F10", {"entities" : qUnion([Q0]), "operationType" : NewBodyOperationType.REMOVE, "endBound" : BoundingType.THROUGH_ALL, "oppositeDirection" : true, "depth" : 25.4 * mm, "offsetDistance" : 25.4 * mm});
        }
        {
            var Q0;
            Q0=qSketchRegion(id+"F9",true);
            var Q1;
            Q1=makeQuery(id+"F8.opExtrude","SWEPT_FACE",FACE,{"disambiguationData":[OSD([sQuery(id+"F7.wireOp",EDGE,"E12.top")])]});
            extrude(context, id + "F11", {"entities" : qUnion([Q0]), "operationType" : NewBodyOperationType.ADD, "endBound" : BoundingType.UP_TO_SURFACE, "oppositeDirection" : true, "depth" : 25.4 * mm, "endBoundEntityFace" : qUnion([Q1]), "offsetDistance" : 25.4 * mm});
        }
        {
            var Q0;
            Q0=makeQuery(id+"F11.boolean.opBoolean","MERGE",FACE,{"derivedFrom":[makeQuery(id+"F8.opExtrude","SWEPT_FACE",FACE,{"disambiguationData":[OSD([sQuery(id+"F7.wireOp",EDGE,"E12.bottom")])]}),makeQuery(id+"F11.opExtrude","CAP_FACE",FACE,{"disambiguationData":[OSD([sQuery(id+"F9.wireOp",EDGE,"E13"),sQuery(id+"F9.wireOp",EDGE,"E14")])],"isStart":true})]});
            var sketch = newSketch(context, id + "F12", { "sketchPlane" : qUnion([Q0])});
            skCircle(sketch, "E15", {"center": v(78.36, 2.03) * mm, "radius": 2.03 * mm});
            skCircle(sketch, "E16", {"center": v(78.36, 2.03) * mm, "radius": 0.89 * mm});
            skLineSegment(sketch, "E17", {"start": v(78.36, 0) * mm, "end": v(76.2, 0) * mm});
            skLineSegment(sketch, "E18", {"start": v(76.2, 2.29) * mm, "end": v(76.34, 2.29) * mm});
            skSolve(sketch);
        }
        {
            var Q0;
            Q0=makeQuery(id+"F12.imprint","IMPRINT",FACE,{"disambiguationData":[TD([[makeQuery(id+"F12.imprint","IMPRINT",EDGE,{"derivedFrom":sQuery(id+"F12.wireOp",EDGE,"E16")}),-1.0]])]});
            var Q1;
            {var subQ0=sQuery(id+"F12.wireOp",EDGE,"E17");Q1=makeQuery(id+"F12.imprint","IMPRINT",FACE,{"disambiguationData":[TD([[makeQuery(id+"F12.imprint","IMPRINT",EDGE,{"derivedFrom":subQ0}),-1.0]])]});}
            extrude(context, id + "F13", {"entities" : qUnion([Q0, Q1]), "operationType" : NewBodyOperationType.ADD, "oppositeDirection" : true, "depth" : 7.62 * mm, "offsetDistance" : 25.4 * mm});
        }
        {
            var Q0;
            {var subQ0=sQuery(id+"F7.wireOp",EDGE,"E12.top");Q0=makeQuery(id+"F11.boolean.opBoolean","MERGE",FACE,{"derivedFrom":[makeQuery(id+"F8.opExtrude","SWEPT_FACE",FACE,{"disambiguationData":[OSD([subQ0])]}),makeQuery(id+"F11.opExtrude","CAP_FACE",FACE,{"disambiguationData":[OSD([subQ0])],"isStart":false})]});}
            var sketch = newSketch(context, id + "F14", { "sketchPlane" : qUnion([Q0])});
            skCircle(sketch, "E19.0", {"center": v(-78.36, 2.03) * mm, "radius": 0.89 * mm});
            skArc(sketch, "E20.0", {"start": v(-78.36, 0) * mm, "mid": v(-79.88, 3.38) * mm, "end": v(-76.34, 2.29) * mm});
            skCircle(sketch, "E21", {"center": v(-78.36, 2.03) * mm, "radius": 2.03 * mm});
            skLineSegment(sketch, "E22", {"start": v(-76.34, 2.29) * mm, "end": v(-76.2, 2.29) * mm});
            skLineSegment(sketch, "E23", {"start": v(-76.2, 2.29) * mm, "end": v(-76.2, 0) * mm});
            skLineSegment(sketch, "E24", {"start": v(-76.2, 0) * mm, "end": v(-78.36, 0) * mm});
            skSolve(sketch);
        }
        {
            var Q0;
            Q0=qSketchRegion(id+"F14",true);
            extrude(context, id + "F15", {"entities" : qUnion([Q0]), "operationType" : NewBodyOperationType.ADD, "oppositeDirection" : true, "depth" : 7.62 * mm, "offsetDistance" : 25.4 * mm});
        }
        {
            var Q0;
            Q0=qCreatedBy(makeId("Top.planeOp"),FACE);
            var sketch = newSketch(context, id + "F16", { "sketchPlane" : qUnion([Q0])});
            skLineSegment(sketch, "E25.bottom", {"start": v(89.03, 33.27) * mm, "end": v(109.35, 33.27) * mm});
            skLineSegment(sketch, "E25.top", {"start": v(89.03, 28.2) * mm, "end": v(109.35, 28.2) * mm});
            skLineSegment(sketch, "E25.left", {"start": v(89.03, 33.27) * mm, "end": v(89.03, 28.2) * mm});
            skLineSegment(sketch, "E25.right", {"start": v(109.35, 33.27) * mm, "end": v(109.35, 28.2) * mm});
            skPoint(sketch, "E25.middle", {"position": v(99.19, 30.73) * mm});
            skLineSegment(sketch, "E26.0", {"start": v(86.74, 35.56) * mm, "end": v(111.63, 35.56) * mm});
            skLineSegment(sketch, "E26.1", {"start": v(86.74, 35.56) * mm, "end": v(86.74, 25.9) * mm});
            skLineSegment(sketch, "E26.2", {"start": v(86.74, 25.9) * mm, "end": v(111.63, 25.9) * mm});
            skLineSegment(sketch, "E26.3", {"start": v(111.63, 35.56) * mm, "end": v(111.63, 25.9) * mm});
            skLineSegment(sketch, "E27.0", {"start": v(80.4, 25.9) * mm, "end": v(76.34, 25.9) * mm});
            skSolve(sketch);
        }
        {
            var Q0;
            Q0=qSketchRegion(id+"F16",true);
            extrude(context, id + "F17", {"entities" : qUnion([Q0]), "depth" : 10.16 * mm, "offsetDistance" : 25.4 * mm});
        }
        {
            var Q0;
            Q0=makeQuery(id+"F15.boolean.opBoolean","MERGE",FACE,{"derivedFrom":[makeQuery(id+"F13.boolean.opBoolean","MERGE",FACE,{"derivedFrom":[makeQuery(id+"F8.opExtrude","CAP_FACE",FACE,{"disambiguationData":[OSD([sQuery(id+"F7.wireOp",EDGE,"E12.bottom"),sQuery(id+"F7.wireOp",EDGE,"E12.top"),sQuery(id+"F7.wireOp",EDGE,"E12.left"),sQuery(id+"F7.wireOp",EDGE,"E12.right")])],"isStart":true}),makeQuery(id+"F13.opExtrude","SWEPT_FACE",FACE,{"disambiguationData":[OSD([sQuery(id+"F12.wireOp",EDGE,"E17")])]})]}),makeQuery(id+"F15.opExtrude","SWEPT_FACE",FACE,{"disambiguationData":[OSD([sQuery(id+"F14.wireOp",EDGE,"E24")])]})]});
            var sketch = newSketch(context, id + "F18", { "sketchPlane" : qUnion([Q0])});
            skLineSegment(sketch, "E28.bottom", {"start": v(-0.76, -27.69) * mm, "end": v(0.76, -27.69) * mm});
            skLineSegment(sketch, "E28.top", {"start": v(-0.76, -31.5) * mm, "end": v(0.76, -31.5) * mm});
            skLineSegment(sketch, "E28.left", {"start": v(-0.76, -27.69) * mm, "end": v(-0.76, -31.5) * mm});
            skLineSegment(sketch, "E28.right", {"start": v(0.76, -27.69) * mm, "end": v(0.76, -31.5) * mm});
            skPoint(sketch, "E28.middle", {"position": v(0, -29.6) * mm});
            skSolve(sketch);
        }
        {
            var Q0;
            Q0=qSketchRegion(id+"F18",true);
            extrude(context, id + "F19", {"entities" : qUnion([Q0]), "operationType" : NewBodyOperationType.REMOVE, "endBound" : BoundingType.UP_TO_NEXT, "oppositeDirection" : true, "depth" : 25.4 * mm, "offsetDistance" : 25.4 * mm});
        }
        {
            var Q0;
            Q0=makeQuery(id+"F13.boolean.opBoolean","MERGE",EDGE,{"derivedFrom":[makeQuery(id+"F8.opExtrude","CAP_EDGE",EDGE,{"disambiguationData":[OSD([sQuery(id+"F7.wireOp",EDGE,"E12.bottom")])],"isStart":false}),makeQuery(id+"F13.opExtrude","CAP_EDGE",EDGE,{"disambiguationData":[OSD([sQuery(id+"F12.wireOp",EDGE,"E18")])],"isStart":true})]});
            var Q1;
            Q1=makeQuery(id+"F13.boolean.opBoolean","MERGE",EDGE,{"derivedFrom":[makeQuery(id+"F8.opExtrude","CAP_EDGE",EDGE,{"disambiguationData":[OSD([sQuery(id+"F7.wireOp",EDGE,"E12.bottom")])],"isStart":true}),makeQuery(id+"F13.opExtrude","CAP_EDGE",EDGE,{"disambiguationData":[OSD([sQuery(id+"F12.wireOp",EDGE,"E17")])],"isStart":true})]});
            var Q2;
            Q2=makeQuery(id+"F15.boolean.opBoolean","MERGE",EDGE,{"derivedFrom":[makeQuery(id+"F8.opExtrude","CAP_EDGE",EDGE,{"disambiguationData":[OSD([sQuery(id+"F7.wireOp",EDGE,"E12.top")])],"isStart":false}),makeQuery(id+"F15.opExtrude","CAP_EDGE",EDGE,{"disambiguationData":[OSD([sQuery(id+"F14.wireOp",EDGE,"E22")])],"isStart":true})]});
            var Q3;
            Q3=makeQuery(id+"F15.boolean.opBoolean","MERGE",EDGE,{"derivedFrom":[makeQuery(id+"F8.opExtrude","CAP_EDGE",EDGE,{"disambiguationData":[OSD([sQuery(id+"F7.wireOp",EDGE,"E12.top")])],"isStart":true}),makeQuery(id+"F15.opExtrude","CAP_EDGE",EDGE,{"disambiguationData":[OSD([sQuery(id+"F14.wireOp",EDGE,"E24")])],"isStart":true})]});
            var Q4;
            Q4=makeQuery(id+"F1.opExtrude","CAP_EDGE",EDGE,{"disambiguationData":[OSD([sQuery(id+"F0.wireOp",EDGE,"E0.bottom")])],"isStart":true});
            var Q5;
            Q5=makeQuery(id+"F1.opExtrude","CAP_EDGE",EDGE,{"disambiguationData":[OSD([sQuery(id+"F0.wireOp",EDGE,"E0.bottom")])],"isStart":false});
            var Q6;
            Q6=makeQuery(id+"F17.opExtrude","CAP_EDGE",EDGE,{"disambiguationData":[OSD([sQuery(id+"F16.wireOp",EDGE,"E26.2")])],"isStart":true});
            var Q7;
            Q7=makeQuery(id+"F17.opExtrude","CAP_EDGE",EDGE,{"disambiguationData":[OSD([sQuery(id+"F16.wireOp",EDGE,"E26.3")])],"isStart":true});
            var Q8;
            Q8=makeQuery(id+"F17.opExtrude","CAP_EDGE",EDGE,{"disambiguationData":[OSD([sQuery(id+"F16.wireOp",EDGE,"E26.0")])],"isStart":true});
            var Q9;
            Q9=makeQuery(id+"F17.opExtrude","CAP_EDGE",EDGE,{"disambiguationData":[OSD([sQuery(id+"F16.wireOp",EDGE,"E26.1")])],"isStart":true});
            var Q10;
            Q10=makeQuery(id+"F17.opExtrude","CAP_EDGE",EDGE,{"disambiguationData":[OSD([sQuery(id+"F16.wireOp",EDGE,"E26.1")])],"isStart":false});
            var Q11;
            Q11=makeQuery(id+"F17.opExtrude","CAP_EDGE",EDGE,{"disambiguationData":[OSD([sQuery(id+"F16.wireOp",EDGE,"E26.0")])],"isStart":false});
            var Q12;
            Q12=makeQuery(id+"F17.opExtrude","CAP_EDGE",EDGE,{"disambiguationData":[OSD([sQuery(id+"F16.wireOp",EDGE,"E26.2")])],"isStart":false});
            var Q13;
            Q13=makeQuery(id+"F17.opExtrude","CAP_EDGE",EDGE,{"disambiguationData":[OSD([sQuery(id+"F16.wireOp",EDGE,"E26.3")])],"isStart":false});
            var Q14;
            Q14=makeQuery(id+"F8.opExtrude","CAP_EDGE",EDGE,{"disambiguationData":[OSD([sQuery(id+"F7.wireOp",EDGE,"E12.right")])],"isStart":true});
            var Q15;
            Q15=makeQuery(id+"F8.opExtrude","CAP_EDGE",EDGE,{"disambiguationData":[OSD([sQuery(id+"F7.wireOp",EDGE,"E12.right")])],"isStart":false});
            var Q16;
            Q16=makeQuery(id+"F17.opExtrude","SWEPT_EDGE",EDGE,{"disambiguationData":[OSD([sQuery(id+"F16.wireOp",EDGE,"E26.0"),sQuery(id+"F16.wireOp",EDGE,"E26.3")])]});
            var Q17;
            Q17=makeQuery(id+"F17.opExtrude","SWEPT_EDGE",EDGE,{"disambiguationData":[OSD([sQuery(id+"F16.wireOp",EDGE,"E26.0"),sQuery(id+"F16.wireOp",EDGE,"E26.1")])]});
            var Q18;
            Q18=makeQuery(id+"F17.opExtrude","SWEPT_EDGE",EDGE,{"disambiguationData":[OSD([sQuery(id+"F16.wireOp",EDGE,"E26.2"),sQuery(id+"F16.wireOp",EDGE,"E26.3")])]});
            var Q19;
            Q19=makeQuery(id+"F17.opExtrude","SWEPT_EDGE",EDGE,{"disambiguationData":[OSD([sQuery(id+"F16.wireOp",EDGE,"E26.1"),sQuery(id+"F16.wireOp",EDGE,"E26.2")])]});
            fillet(context, id + "F20", {"entities" : qUnion([Q0, Q1, Q2, Q3, Q4, Q5, Q6, Q7, Q8, Q9, Q10, Q11, Q12, Q13, Q14, Q15, Q16, Q17, Q18, Q19]), "radius" : 1.14 * mm, "tangentPropagation" : true, "allowEdgeOverflow" : false});
        }
        {
            var Q0;
            Q0=makeQuery(id+"F17.opExtrude","SWEPT_BODY",BODY,{"disambiguationData":[OSD([sQuery(id+"F16.wireOp",EDGE,"E25.bottom"),sQuery(id+"F16.wireOp",EDGE,"E25.top"),sQuery(id+"F16.wireOp",EDGE,"E25.left"),sQuery(id+"F16.wireOp",EDGE,"E25.right"),sQuery(id+"F16.wireOp",EDGE,"E26.0"),sQuery(id+"F16.wireOp",EDGE,"E26.1"),sQuery(id+"F16.wireOp",EDGE,"E26.2"),sQuery(id+"F16.wireOp",EDGE,"E26.3")])]});
            deleteBodies(context, id + "F21", {"entities" : qUnion([Q0])});
        }
        {
            var Q0;
            Q0=makeQuery(id+"F1.opExtrude","SWEPT_BODY",BODY,{"disambiguationData":[OSD([sQuery(id+"F0.wireOp",EDGE,"E0.bottom"),sQuery(id+"F0.wireOp",EDGE,"E0.top"),sQuery(id+"F0.wireOp",EDGE,"E0.left"),sQuery(id+"F0.wireOp",EDGE,"E0.right"),sQuery(id+"F0.wireOp",EDGE,"E1.filletArc"),sQuery(id+"F0.wireOp",EDGE,"E2.filletArc"),sQuery(id+"F0.wireOp",EDGE,"E3.bottom"),sQuery(id+"F0.wireOp",EDGE,"E3.top"),sQuery(id+"F0.wireOp",EDGE,"E3.left"),sQuery(id+"F0.wireOp",EDGE,"E3.right"),sQuery(id+"F0.wireOp",EDGE,"E4.filletArc"),sQuery(id+"F0.wireOp",EDGE,"E5.filletArc"),sQuery(id+"F0.wireOp",EDGE,"E6.filletArc"),sQuery(id+"F0.wireOp",EDGE,"E7.filletArc"),sQuery(id+"F0.wireOp",EDGE,"E8.1.0.5"),sQuery(id+"F0.wireOp",EDGE,"E8.1.0.6"),sQuery(id+"F0.wireOp",EDGE,"E8.1.0.7"),sQuery(id+"F0.wireOp",EDGE,"E8.1.0.8"),sQuery(id+"F0.wireOp",EDGE,"E8.1.0.9"),sQuery(id+"F0.wireOp",EDGE,"E8.1.0.10"),sQuery(id+"F0.wireOp",EDGE,"E8.1.0.11"),sQuery(id+"F0.wireOp",EDGE,"E8.1.0.12"),sQuery(id+"F0.wireOp",EDGE,"E8.2.0.5"),sQuery(id+"F0.wireOp",EDGE,"E8.2.0.6"),sQuery(id+"F0.wireOp",EDGE,"E8.2.0.7"),sQuery(id+"F0.wireOp",EDGE,"E8.2.0.8"),sQuery(id+"F0.wireOp",EDGE,"E8.2.0.9"),sQuery(id+"F0.wireOp",EDGE,"E8.2.0.10"),sQuery(id+"F0.wireOp",EDGE,"E8.2.0.11"),sQuery(id+"F0.wireOp",EDGE,"E8.2.0.12"),sQuery(id+"F0.wireOp",EDGE,"E8.3.0.5"),sQuery(id+"F0.wireOp",EDGE,"E8.3.0.6"),sQuery(id+"F0.wireOp",EDGE,"E8.3.0.7"),sQuery(id+"F0.wireOp",EDGE,"E8.3.0.8"),sQuery(id+"F0.wireOp",EDGE,"E8.3.0.9"),sQuery(id+"F0.wireOp",EDGE,"E8.3.0.10"),sQuery(id+"F0.wireOp",EDGE,"E8.3.0.11"),sQuery(id+"F0.wireOp",EDGE,"E8.3.0.12"),sQuery(id+"F0.wireOp",EDGE,"E8.4.0.5"),sQuery(id+"F0.wireOp",EDGE,"E8.4.0.6"),sQuery(id+"F0.wireOp",EDGE,"E8.4.0.7"),sQuery(id+"F0.wireOp",EDGE,"E8.4.0.8"),sQuery(id+"F0.wireOp",EDGE,"E8.4.0.9"),sQuery(id+"F0.wireOp",EDGE,"E8.4.0.10"),sQuery(id+"F0.wireOp",EDGE,"E8.4.0.11"),sQuery(id+"F0.wireOp",EDGE,"E8.4.0.12"),sQuery(id+"F0.wireOp",EDGE,"E8.5.0.5"),sQuery(id+"F0.wireOp",EDGE,"E8.5.0.6"),sQuery(id+"F0.wireOp",EDGE,"E8.5.0.7"),sQuery(id+"F0.wireOp",EDGE,"E8.5.0.8"),sQuery(id+"F0.wireOp",EDGE,"E8.5.0.9"),sQuery(id+"F0.wireOp",EDGE,"E8.5.0.10"),sQuery(id+"F0.wireOp",EDGE,"E8.5.0.11"),sQuery(id+"F0.wireOp",EDGE,"E8.5.0.12"),sQuery(id+"F0.wireOp",EDGE,"E8.6.0.5"),sQuery(id+"F0.wireOp",EDGE,"E8.6.0.6"),sQuery(id+"F0.wireOp",EDGE,"E8.6.0.7"),sQuery(id+"F0.wireOp",EDGE,"E8.6.0.8"),sQuery(id+"F0.wireOp",EDGE,"E8.6.0.9"),sQuery(id+"F0.wireOp",EDGE,"E8.6.0.10"),sQuery(id+"F0.wireOp",EDGE,"E8.6.0.11"),sQuery(id+"F0.wireOp",EDGE,"E8.6.0.12"),sQuery(id+"F0.wireOp",EDGE,"E8.7.0.5"),sQuery(id+"F0.wireOp",EDGE,"E8.7.0.6"),sQuery(id+"F0.wireOp",EDGE,"E8.7.0.7"),sQuery(id+"F0.wireOp",EDGE,"E8.7.0.8"),sQuery(id+"F0.wireOp",EDGE,"E8.7.0.9"),sQuery(id+"F0.wireOp",EDGE,"E8.7.0.10"),sQuery(id+"F0.wireOp",EDGE,"E8.7.0.11"),sQuery(id+"F0.wireOp",EDGE,"E8.7.0.12"),sQuery(id+"F0.wireOp",EDGE,"E8.8.0.5"),sQuery(id+"F0.wireOp",EDGE,"E8.8.0.6"),sQuery(id+"F0.wireOp",EDGE,"E8.8.0.7"),sQuery(id+"F0.wireOp",EDGE,"E8.8.0.8"),sQuery(id+"F0.wireOp",EDGE,"E8.8.0.9"),sQuery(id+"F0.wireOp",EDGE,"E8.8.0.10"),sQuery(id+"F0.wireOp",EDGE,"E8.8.0.11"),sQuery(id+"F0.wireOp",EDGE,"E8.8.0.12"),sQuery(id+"F0.wireOp",EDGE,"E8.9.0.5"),sQuery(id+"F0.wireOp",EDGE,"E8.9.0.6"),sQuery(id+"F0.wireOp",EDGE,"E8.9.0.7"),sQuery(id+"F0.wireOp",EDGE,"E8.9.0.8"),sQuery(id+"F0.wireOp",EDGE,"E8.9.0.9"),sQuery(id+"F0.wireOp",EDGE,"E8.9.0.10"),sQuery(id+"F0.wireOp",EDGE,"E8.9.0.11"),sQuery(id+"F0.wireOp",EDGE,"E8.9.0.12"),sQuery(id+"F0.wireOp",EDGE,"E8.10.0.5"),sQuery(id+"F0.wireOp",EDGE,"E8.10.0.6"),sQuery(id+"F0.wireOp",EDGE,"E8.10.0.7"),sQuery(id+"F0.wireOp",EDGE,"E8.10.0.8"),sQuery(id+"F0.wireOp",EDGE,"E8.10.0.9"),sQuery(id+"F0.wireOp",EDGE,"E8.10.0.10"),sQuery(id+"F0.wireOp",EDGE,"E8.10.0.11"),sQuery(id+"F0.wireOp",EDGE,"E8.10.0.12"),sQuery(id+"F0.wireOp",EDGE,"E8.11.0.5"),sQuery(id+"F0.wireOp",EDGE,"E8.11.0.6"),sQuery(id+"F0.wireOp",EDGE,"E8.11.0.7"),sQuery(id+"F0.wireOp",EDGE,"E8.11.0.8"),sQuery(id+"F0.wireOp",EDGE,"E8.11.0.9"),sQuery(id+"F0.wireOp",EDGE,"E8.11.0.10"),sQuery(id+"F0.wireOp",EDGE,"E8.11.0.11"),sQuery(id+"F0.wireOp",EDGE,"E8.11.0.12"),sQuery(id+"F0.wireOp",EDGE,"E8.12.0.5"),sQuery(id+"F0.wireOp",EDGE,"E8.12.0.6"),sQuery(id+"F0.wireOp",EDGE,"E8.12.0.7"),sQuery(id+"F0.wireOp",EDGE,"E8.12.0.8"),sQuery(id+"F0.wireOp",EDGE,"E8.12.0.9"),sQuery(id+"F0.wireOp",EDGE,"E8.12.0.10"),sQuery(id+"F0.wireOp",EDGE,"E8.12.0.11"),sQuery(id+"F0.wireOp",EDGE,"E8.12.0.12")])]});
            deleteBodies(context, id + "F22", {"entities" : qUnion([Q0])});
        }
    });
